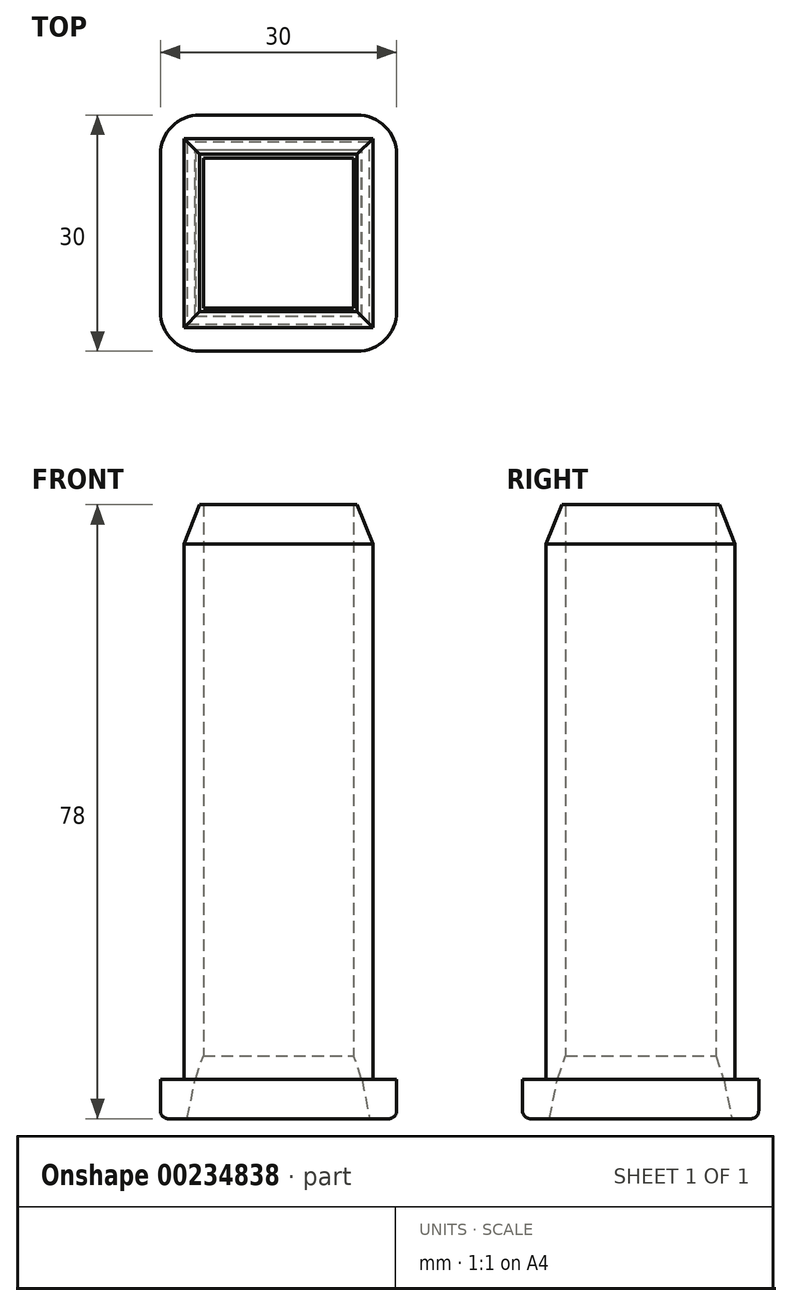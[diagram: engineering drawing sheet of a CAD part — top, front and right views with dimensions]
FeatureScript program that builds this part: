
annotation { "Feature Type Name" : "Feature", "Feature Type Description" : "" }
export const myFeature = defineFeature(function(context is Context, id is Id, definition is map)
    precondition{}
    {
        {
            var Q0;
            Q0=qCreatedBy(makeId("Top.planeOp"),FACE);
            var sketch = newSketch(context, id + "F0", { "sketchPlane" : qUnion([Q0])});
            skLineSegment(sketch, "E0.bottom", {"start": v(-11.07, 13.82) * mm, "end": v(12.93, 13.82) * mm});
            skLineSegment(sketch, "E0.top", {"start": v(-11.07, -10.18) * mm, "end": v(12.93, -10.18) * mm});
            skLineSegment(sketch, "E0.left", {"start": v(-11.07, 13.82) * mm, "end": v(-11.07, -10.18) * mm});
            skLineSegment(sketch, "E0.right", {"start": v(12.93, 13.82) * mm, "end": v(12.93, -10.18) * mm});
            skLineSegment(sketch, "E1.bottom", {"start": v(-8.62, 11.37) * mm, "end": v(10.48, 11.37) * mm});
            skLineSegment(sketch, "E1.top", {"start": v(-8.62, -7.73) * mm, "end": v(10.48, -7.73) * mm});
            skLineSegment(sketch, "E1.left", {"start": v(-8.62, 11.37) * mm, "end": v(-8.62, -7.73) * mm});
            skLineSegment(sketch, "E1.right", {"start": v(10.48, 11.37) * mm, "end": v(10.48, -7.73) * mm});
            skSolve(sketch);
        }
        {
            var Q0;
            Q0 = qSketchRegion(id + "F0", true);
            extrude(context, id + "F1", {"entities" : qUnion([Q0]), "depth" : 73 * mm});
        }
        {
            var Q0;
            Q0=qCreatedBy(makeId("Top.planeOp"),FACE);
            var sketch = newSketch(context, id + "F2", { "sketchPlane" : qUnion([Q0])});
            skLineSegment(sketch, "E2.bottom", {"start": v(-14.07, -13.18) * mm, "end": v(15.93, -13.18) * mm});
            skLineSegment(sketch, "E2.top", {"start": v(-14.07, 16.82) * mm, "end": v(15.93, 16.82) * mm});
            skLineSegment(sketch, "E2.left", {"start": v(-14.07, -13.18) * mm, "end": v(-14.07, 16.82) * mm});
            skLineSegment(sketch, "E2.right", {"start": v(15.93, -13.18) * mm, "end": v(15.93, 16.82) * mm});
            skLineSegment(sketch, "E3.bottom", {"start": v(-8.66, -7.75) * mm, "end": v(10.5, -7.75) * mm});
            skLineSegment(sketch, "E3.top", {"start": v(-8.66, 11.4) * mm, "end": v(10.5, 11.4) * mm});
            skLineSegment(sketch, "E3.left", {"start": v(-8.66, -7.75) * mm, "end": v(-8.66, 11.4) * mm});
            skLineSegment(sketch, "E3.right", {"start": v(10.5, -7.75) * mm, "end": v(10.5, 11.4) * mm});
            skSolve(sketch);
        }
        {
            var Q0;
            Q0 = qSketchRegion(id + "F2", true);
            extrude(context, id + "F3", {"entities" : qUnion([Q0]), "operationType" : NewBodyOperationType.ADD, "oppositeDirection" : true, "depth" : 5 * mm});
        }
        {
            var Q0;
            Q0=makeQuery(id+"F3.opExtrude","CAP_EDGE",EDGE,{"disambiguationData":[OSD([sQuery(id+"F2.wireOp",EDGE,"E3.bottom")])],"isStart":false});
            var Q1;
            Q1=makeQuery(id+"F3.opExtrude","CAP_EDGE",EDGE,{"disambiguationData":[OSD([sQuery(id+"F2.wireOp",EDGE,"E3.right")])],"isStart":false});
            var Q2;
            Q2=makeQuery(id+"F3.opExtrude","CAP_EDGE",EDGE,{"disambiguationData":[OSD([sQuery(id+"F2.wireOp",EDGE,"E3.top")])],"isStart":false});
            var Q3;
            Q3=makeQuery(id+"F3.opExtrude","CAP_EDGE",EDGE,{"disambiguationData":[OSD([sQuery(id+"F2.wireOp",EDGE,"E3.left")])],"isStart":false});
            chamfer(context, id + "F4", {"entities" : qUnion([Q0, Q1, Q2, Q3]), "chamferType" : ChamferType.TWO_OFFSETS, "width1" : 2 * mm, "oppositeDirection" : false, "width2" : 10 * mm, "tangentPropagation" : true});
        }
        {
            var Q0;
            Q0=makeQuery(id+"F1.opExtrude","CAP_EDGE",EDGE,{"disambiguationData":[OSD([sQuery(id+"F0.wireOp",EDGE,"E1.top")])],"isStart":true});
            var Q1;
            Q1=makeQuery(id+"F1.opExtrude","CAP_EDGE",EDGE,{"disambiguationData":[OSD([sQuery(id+"F0.wireOp",EDGE,"E1.right")])],"isStart":true});
            var Q2;
            Q2=makeQuery(id+"F1.opExtrude","CAP_EDGE",EDGE,{"disambiguationData":[OSD([sQuery(id+"F0.wireOp",EDGE,"E1.bottom")])],"isStart":true});
            var Q3;
            Q3=makeQuery(id+"F1.opExtrude","CAP_EDGE",EDGE,{"disambiguationData":[OSD([sQuery(id+"F0.wireOp",EDGE,"E1.left")])],"isStart":true});
            chamfer(context, id + "F5", {"entities" : qUnion([Q0, Q1, Q2, Q3]), "chamferType" : ChamferType.TWO_OFFSETS, "width1" : 1 * mm, "oppositeDirection" : false, "width2" : 3 * mm, "tangentPropagation" : true});
        }
        {
            var Q0;
            Q0=makeQuery(id+"F3.opExtrude","SWEPT_EDGE",EDGE,{"disambiguationData":[OSD([sQuery(id+"F2.wireOp",EDGE,"E2.top"),sQuery(id+"F2.wireOp",EDGE,"E2.left")])]});
            var Q1;
            Q1=makeQuery(id+"F3.opExtrude","SWEPT_EDGE",EDGE,{"disambiguationData":[OSD([sQuery(id+"F2.wireOp",EDGE,"E2.top"),sQuery(id+"F2.wireOp",EDGE,"E2.right")])]});
            var Q2;
            Q2=makeQuery(id+"F3.opExtrude","SWEPT_EDGE",EDGE,{"disambiguationData":[OSD([sQuery(id+"F2.wireOp",EDGE,"E2.bottom"),sQuery(id+"F2.wireOp",EDGE,"E2.right")])]});
            var Q3;
            Q3=makeQuery(id+"F3.opExtrude","SWEPT_EDGE",EDGE,{"disambiguationData":[OSD([sQuery(id+"F2.wireOp",EDGE,"E2.bottom"),sQuery(id+"F2.wireOp",EDGE,"E2.left")])]});
            fillet(context, id + "F6", {"entities" : qUnion([Q0, Q1, Q2, Q3]), "radius" : 5 * mm, "tangentPropagation" : true, "allowEdgeOverflow" : false});
        }
        {
            var Q0;
            Q0=makeQuery(id+"F3.opExtrude","CAP_EDGE",EDGE,{"disambiguationData":[OSD([sQuery(id+"F2.wireOp",EDGE,"E2.right")])],"isStart":false});
            var Q1;
            {var subQ0=sQuery(id+"F2.wireOp",EDGE,"E2.right");var subQ1=sQuery(id+"F2.wireOp",EDGE,"E2.bottom");Q1=makeQuery(id+"F6.opFillet","BLEND_EDGE",EDGE,{"blendedFrom":[makeQuery(id+"F3.opExtrude","SWEPT_EDGE",EDGE,{"disambiguationData":[OSD([subQ1,subQ0])]}),makeQuery(id+"F3.opExtrude","CAP_FACE",FACE,{"disambiguationData":[OSD([subQ1,sQuery(id+"F2.wireOp",EDGE,"E2.top"),sQuery(id+"F2.wireOp",EDGE,"E2.left"),subQ0,sQuery(id+"F2.wireOp",EDGE,"E3.bottom"),sQuery(id+"F2.wireOp",EDGE,"E3.top"),sQuery(id+"F2.wireOp",EDGE,"E3.left"),sQuery(id+"F2.wireOp",EDGE,"E3.right")])],"isStart":false})],"blendedInto":[makeQuery(id+"F3.opExtrude","CAP_FACE",FACE,{"disambiguationData":[OSD([subQ1,sQuery(id+"F2.wireOp",EDGE,"E2.top"),sQuery(id+"F2.wireOp",EDGE,"E2.left"),subQ0,sQuery(id+"F2.wireOp",EDGE,"E3.bottom"),sQuery(id+"F2.wireOp",EDGE,"E3.top"),sQuery(id+"F2.wireOp",EDGE,"E3.left"),sQuery(id+"F2.wireOp",EDGE,"E3.right")])],"isStart":false})]});}
            var Q2;
            Q2=makeQuery(id+"F3.opExtrude","CAP_EDGE",EDGE,{"disambiguationData":[OSD([sQuery(id+"F2.wireOp",EDGE,"E2.bottom")])],"isStart":false});
            fillet(context, id + "F7", {"entities" : qUnion([Q0, Q1, Q2]), "radius" : 1 * mm, "tangentPropagation" : true, "allowEdgeOverflow" : false});
        }
        {
            var Q0;
            Q0=makeQuery(id+"F1.opExtrude","CAP_EDGE",EDGE,{"disambiguationData":[OSD([sQuery(id+"F0.wireOp",EDGE,"E0.bottom")])],"isStart":false});
            var Q1;
            Q1=makeQuery(id+"F1.opExtrude","CAP_EDGE",EDGE,{"disambiguationData":[OSD([sQuery(id+"F0.wireOp",EDGE,"E0.right")])],"isStart":false});
            var Q2;
            Q2=makeQuery(id+"F1.opExtrude","CAP_EDGE",EDGE,{"disambiguationData":[OSD([sQuery(id+"F0.wireOp",EDGE,"E0.top")])],"isStart":false});
            var Q3;
            Q3=makeQuery(id+"F1.opExtrude","CAP_EDGE",EDGE,{"disambiguationData":[OSD([sQuery(id+"F0.wireOp",EDGE,"E0.left")])],"isStart":false});
            chamfer(context, id + "F8", {"entities" : qUnion([Q0, Q1, Q2, Q3]), "chamferType" : ChamferType.TWO_OFFSETS, "width1" : 5 * mm, "oppositeDirection" : false, "width2" : 2 * mm, "tangentPropagation" : true});
        }
    });
